# Revit family: Shower_Bases-American_Standard-Townsend-6030SMLHOL_RHOL
name_source: partatom
category: Plumbing Fixtures
revit_build: Autodesk Revit 2014 (Build: 20130308_1515(x64)
units: mm (PartAtom-declared; Revit-internal decimal feet)

## types (2) — shared parameters
CWFU = 1.5
Default Elevation = 0"
Finish = Solid Surface-American Standard-White
HW Connection = No
HWFU = 1.5
Installation Type = Floor Mounted
Length = 30"
Manufacturer = American Standard
Material = Solid Surface-American Standard-White
Price = Prices may vary. Please consult Manufacturer Representative for most up-to-date price list.
Product Documentation Link = https://www.americanstandard-us.com
Product Page URL = https://www.americanstandard-us.com
URL = https://www.americanstandard-us.com
Vent Connection = No
WFU = 3
Warranty Information = Limited Lifetime Warranty
Waste Connection = Yes
Waste Connection Diameter = 3 1/4"
Weight (kg) = 50.5 Kg. (111 Lbs.)
Width = 60"

## per-type parameters (varying)
| type | Assembly Code | CW Connection | Description | Drain Line | L/R | Waste Location |
| 6030SMLHOL | D2010700 | No | Townsend® 60" X 30" Shower Base Solid Surface Left Side Drain | 5 1/2" | 0.00° | 4" |
| 6030SMRHOL | D2010430 | Yes | Townsend® 60" X 30" Shower Base Solid Surface Right Side Drain | 51 5/8" | 180.00° | 56" |

note: column(s) folded — value = type name in every type: Model

## geometry (parser evidence)
native form markers: Sweep x1
no freeform markers — native parametric forms only
